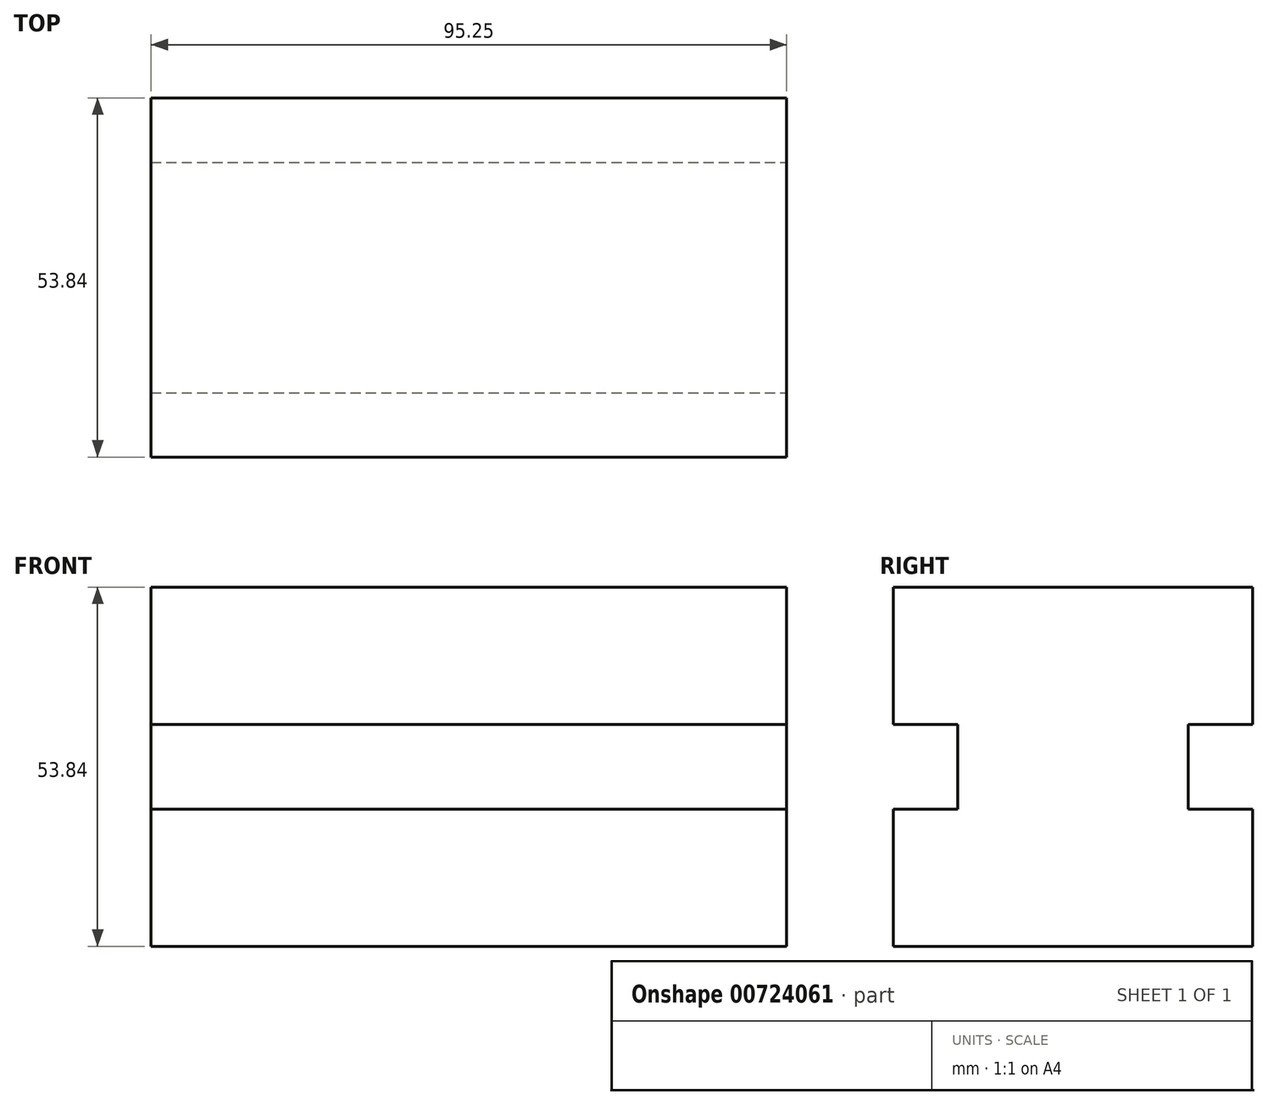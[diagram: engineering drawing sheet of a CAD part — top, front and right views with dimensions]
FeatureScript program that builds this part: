
annotation { "Feature Type Name" : "Feature", "Feature Type Description" : "" }
export const myFeature = defineFeature(function(context is Context, id is Id, definition is map)
    precondition{}
    {
        {
            var Q0;
            Q0=qCreatedBy(makeId("Right.planeOp"),FACE);
            var sketch = newSketch(context, id + "F0", { "sketchPlane" : qUnion([Q0])});
            skLineSegment(sketch, "E0.bottom", {"start": v(26.92, -26.92) * mm, "end": v(-26.92, -26.92) * mm});
            skLineSegment(sketch, "E0.top", {"start": v(26.92, 26.92) * mm, "end": v(-26.92, 26.92) * mm});
            skLineSegment(sketch, "E0.left", {"start": v(26.92, -26.92) * mm, "end": v(26.92, -6.35) * mm});
            skLineSegment(sketch, "E0.right", {"start": v(-26.92, -26.92) * mm, "end": v(-26.92, -6.35) * mm});
            skPoint(sketch, "E0.middle", {"position": v(0, 0) * mm});
            skLineSegment(sketch, "E1.bottom", {"start": v(-26.92, 6.35) * mm, "end": v(-17.27, 6.35) * mm});
            skLineSegment(sketch, "E1.top", {"start": v(-26.92, -6.35) * mm, "end": v(-17.27, -6.35) * mm});
            skLineSegment(sketch, "E1.right", {"start": v(-17.27, 6.35) * mm, "end": v(-17.27, -6.35) * mm});
            skLineSegment(sketch, "E2.trimOffspring", {"start": v(-26.92, 6.35) * mm, "end": v(-26.92, 26.92) * mm});
            skLineSegment(sketch, "E3", {"start": v(0, 34.94) * mm, "end": v(0, -49.76) * mm, "construction": true});
            skLineSegment(sketch, "E4.MirrorCS", {"start": v(17.27, 6.35) * mm, "end": v(17.27, -6.35) * mm});
            skLineSegment(sketch, "E5.MirrorCS", {"start": v(26.92, -6.35) * mm, "end": v(17.27, -6.35) * mm});
            skLineSegment(sketch, "E6.MirrorCS", {"start": v(26.92, 6.35) * mm, "end": v(17.27, 6.35) * mm});
            skLineSegment(sketch, "E7.trimOffspring", {"start": v(26.92, 6.35) * mm, "end": v(26.92, 26.92) * mm});
            skSolve(sketch);
        }
        {
            var Q0;
            Q0=makeQuery(id+"F0.imprint","IMPRINT",FACE,{"disambiguationData":[TD([[makeQuery(id+"F0.imprint","IMPRINT",EDGE,{"derivedFrom":sQuery(id+"F0.wireOp",EDGE,"E0.bottom")}),-1.0]])]});
            extrude(context, id + "F1", {"entities" : qUnion([Q0]), "oppositeDirection" : true, "depth" : 95.25 * mm, "offsetDistance" : 25.4 * mm});
        }
    });
